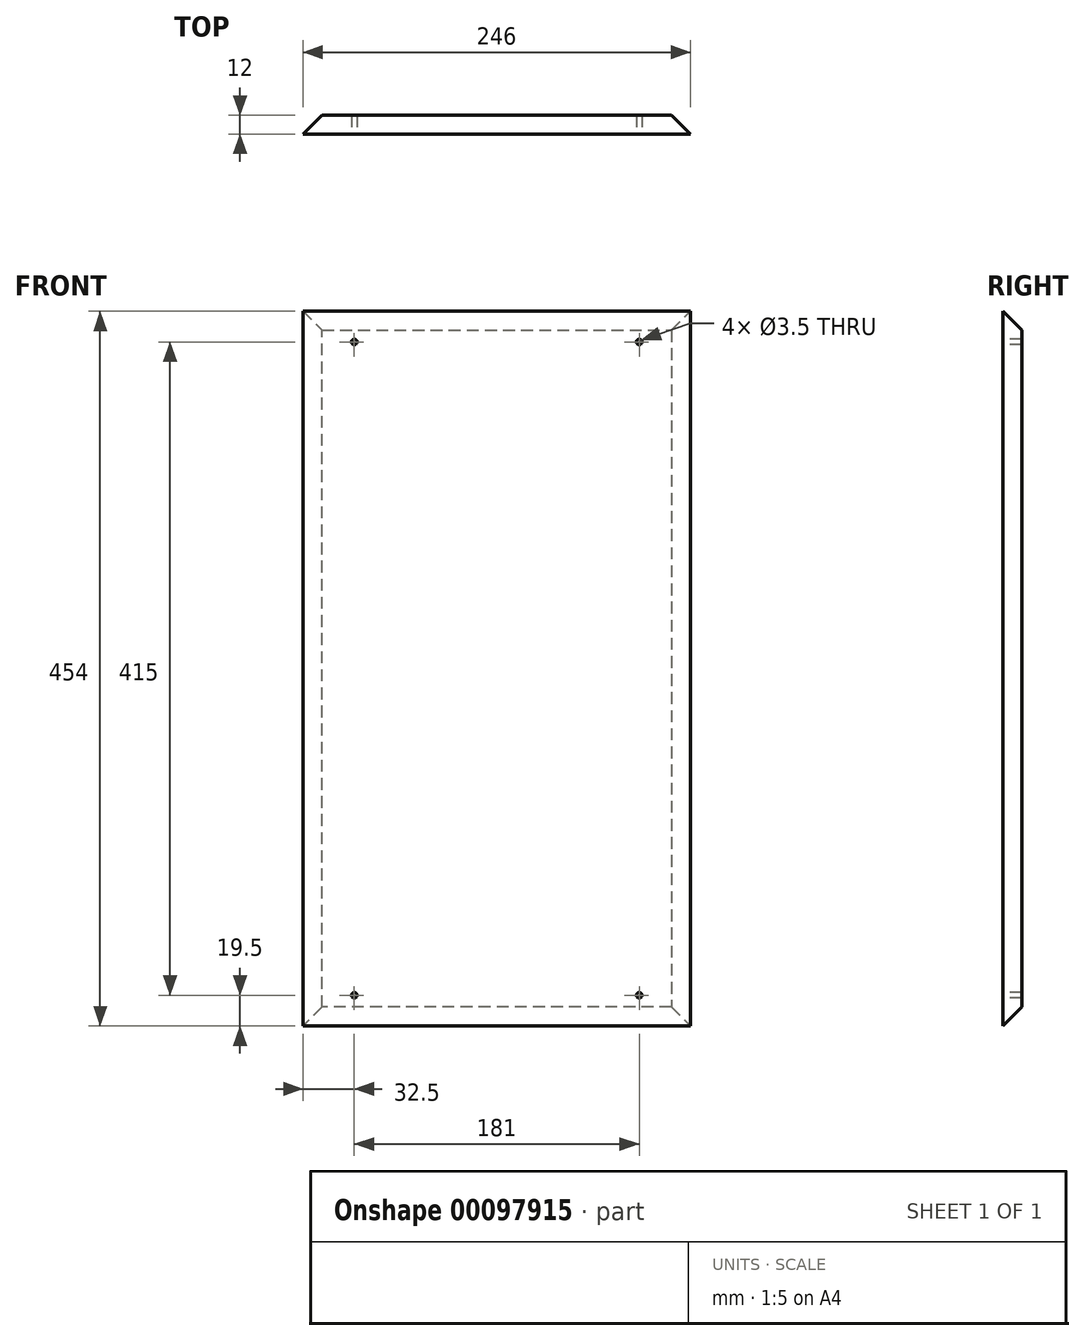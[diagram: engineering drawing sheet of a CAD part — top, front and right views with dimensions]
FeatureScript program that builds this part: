
annotation { "Feature Type Name" : "Feature", "Feature Type Description" : "" }
export const myFeature = defineFeature(function(context is Context, id is Id, definition is map)
    precondition{}
    {
        {
            var Q0;
            Q0=qCreatedBy(makeId("Front.planeOp"),FACE);
            var sketch = newSketch(context, id + "F0", { "sketchPlane" : qUnion([Q0])});
            skLineSegment(sketch, "E0.bottom", {"start": v(-123, 227) * mm, "end": v(123, 227) * mm});
            skLineSegment(sketch, "E0.top", {"start": v(-123, -227) * mm, "end": v(123, -227) * mm});
            skLineSegment(sketch, "E0.left", {"start": v(-123, 227) * mm, "end": v(-123, -227) * mm});
            skLineSegment(sketch, "E0.right", {"start": v(123, 227) * mm, "end": v(123, -227) * mm});
            skSolve(sketch);
        }
        {
            var Q0;
            Q0=makeQuery(id+"F0.imprint","IMPRINT",FACE,{"disambiguationData":[TD([[makeQuery(id+"F0.imprint","IMPRINT",EDGE,{"derivedFrom":sQuery(id+"F0.wireOp",EDGE,"E0.bottom")}),-1.0]])]});
            extrude(context, id + "F1", {"entities" : qUnion([Q0]), "depth" : 12 * mm});
        }
        {
            var Q0;
            Q0=makeQuery(id+"F1.opExtrude","CAP_FACE",FACE,{"disambiguationData":[OSD([sQuery(id+"F0.wireOp",EDGE,"E0.bottom"),sQuery(id+"F0.wireOp",EDGE,"E0.top"),sQuery(id+"F0.wireOp",EDGE,"E0.left"),sQuery(id+"F0.wireOp",EDGE,"E0.right")])],"isStart":true});
            chamfer(context, id + "F2", {"entities" : qUnion([Q0]), "width" : 12 * mm, "tangentPropagation" : true});
        }
        {
            var Q0;
            Q0=makeQuery(id+"F1.opExtrude","CAP_FACE",FACE,{"disambiguationData":[OSD([sQuery(id+"F0.wireOp",EDGE,"E0.bottom"),sQuery(id+"F0.wireOp",EDGE,"E0.top"),sQuery(id+"F0.wireOp",EDGE,"E0.left"),sQuery(id+"F0.wireOp",EDGE,"E0.right")])],"isStart":false});
            var sketch = newSketch(context, id + "F3", { "sketchPlane" : qUnion([Q0])});
            skLineSegment(sketch, "E1.0", {"start": v(-103.5, 207.5) * mm, "end": v(-103.5, -207.5) * mm, "construction": true});
            skLineSegment(sketch, "E1.1", {"start": v(103.5, 207.5) * mm, "end": v(-103.5, 207.5) * mm, "construction": true});
            skLineSegment(sketch, "E1.2", {"start": v(103.5, -207.5) * mm, "end": v(103.5, 207.5) * mm, "construction": true});
            skLineSegment(sketch, "E1.3", {"start": v(-103.5, -207.5) * mm, "end": v(103.5, -207.5) * mm, "construction": true});
            skLineSegment(sketch, "E2.0", {"start": v(-90.5, 194.5) * mm, "end": v(-90.5, -194.5) * mm, "construction": true});
            skLineSegment(sketch, "E2.1", {"start": v(90.5, 194.5) * mm, "end": v(-90.5, 194.5) * mm, "construction": true});
            skLineSegment(sketch, "E2.2", {"start": v(90.5, -194.5) * mm, "end": v(90.5, 194.5) * mm, "construction": true});
            skLineSegment(sketch, "E2.3", {"start": v(-90.5, -194.5) * mm, "end": v(90.5, -194.5) * mm, "construction": true});
            skPoint(sketch, "E3", {"position": v(-90.5, 207.5) * mm});
            skPoint(sketch, "E4", {"position": v(-103.5, 194.5) * mm});
            skPoint(sketch, "E5", {"position": v(103.5, 194.5) * mm});
            skPoint(sketch, "E6", {"position": v(90.5, 207.5) * mm});
            skPoint(sketch, "E7", {"position": v(-103.5, -194.5) * mm});
            skPoint(sketch, "E8", {"position": v(-90.5, -207.5) * mm});
            skPoint(sketch, "E9", {"position": v(103.5, -194.5) * mm});
            skPoint(sketch, "E10", {"position": v(90.5, -207.5) * mm});
            skSolve(sketch);
        }
        {
            var Q0;
            Q0=sQuery(id+"F3.wireOp",VERTEX,"E3");
            var Q1;
            Q1=sQuery(id+"F3.wireOp",VERTEX,"E6");
            var Q2;
            Q2=sQuery(id+"F3.wireOp",VERTEX,"E10");
            var Q3;
            Q3=sQuery(id+"F3.wireOp",VERTEX,"E8");
            var Q4;
            Q4=makeQuery(id+"F1.opExtrude","SWEPT_BODY",BODY,{"disambiguationData":[OSD([sQuery(id+"F0.wireOp",EDGE,"E0.bottom"),sQuery(id+"F0.wireOp",EDGE,"E0.top"),sQuery(id+"F0.wireOp",EDGE,"E0.left"),sQuery(id+"F0.wireOp",EDGE,"E0.right")])]});
            hole(context, id + "F4", {"style" : HoleStyle.SIMPLE, "endStyle" : HoleEndStyle.THROUGH, "holeDiameter" : 3.5 * mm, "locations" : qUnion([Q0, Q1, Q2, Q3]), "scope" : qUnion([Q4]), "isTappedThrough" : true});
        }
    });
